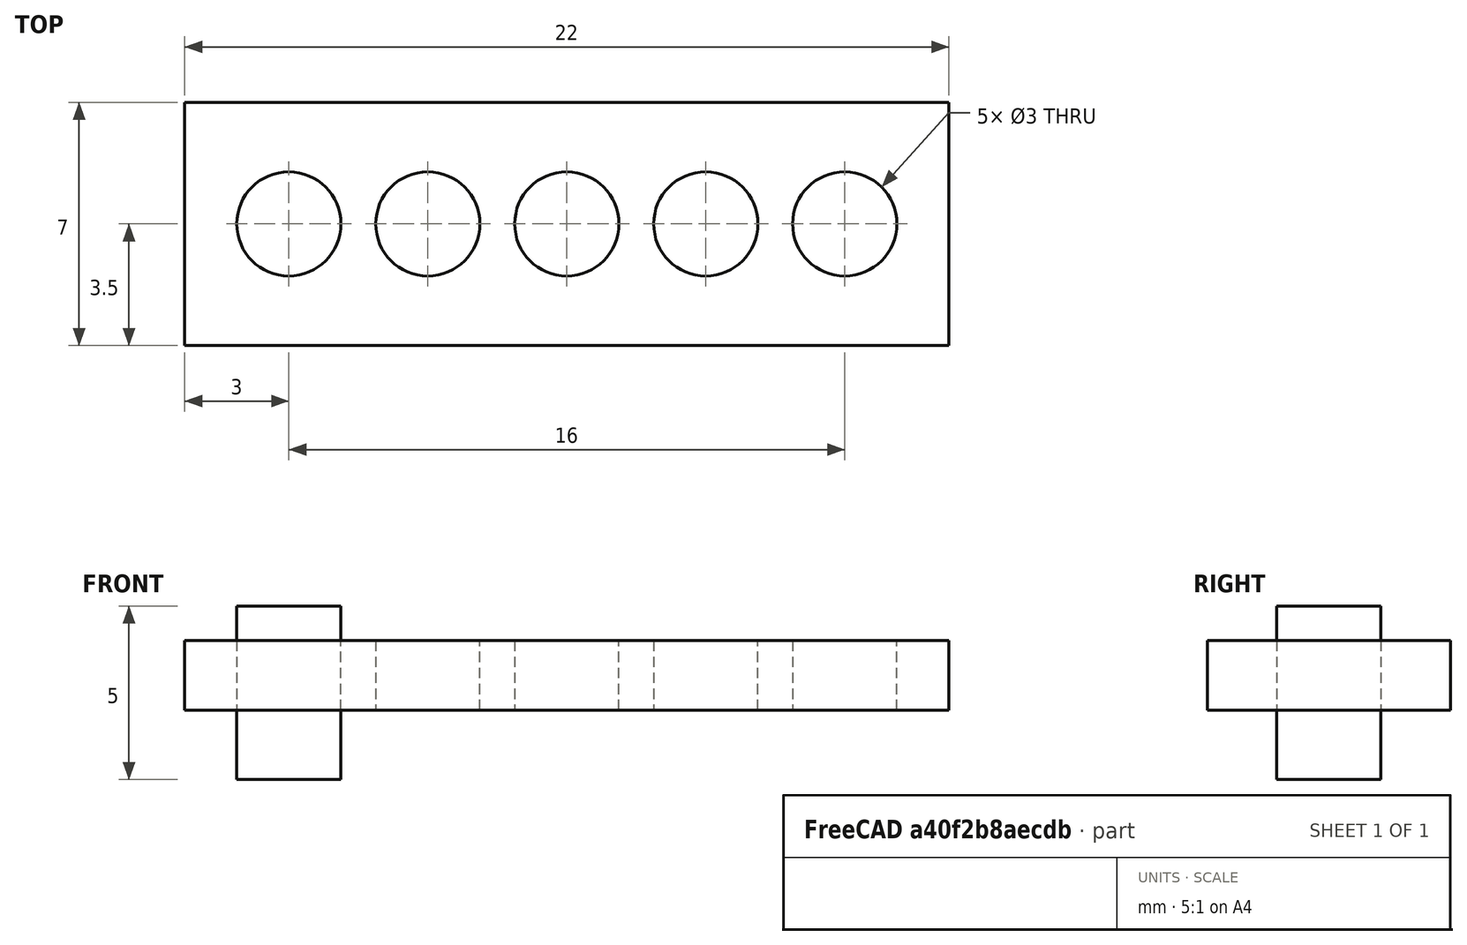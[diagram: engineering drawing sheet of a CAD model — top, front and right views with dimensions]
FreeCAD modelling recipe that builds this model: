
FCSTD DOCUMENT  (FreeCAD 0.21R33694 (Git))
Label: OJT1_T010R09_6cercles_forats
License: All rights reserved
LicenseURL: http://en.wikipedia.org/wiki/All_rights_reserved
objects: Part::Cylinder×1, Part::FeaturePython×1, Part::Box×1, Part::Cut×1
note: 3 computed .brp shape members not serialized (recipe doc carries the construction recipe); baked Part::Feature solids carry a one-line shape summary decoded from their .brp

FEATURE [Part::Cylinder] Cylinder
  Angle = 360
  AttacherType = Attacher::AttachEngine3D
  FirstAngle = 0
  Height = 5
  Radius = 1.5
  SecondAngle = 0
FEATURE [Part::FeaturePython] Array  # Draft array (typed FeaturePython)
  AlwaysSyncPlacement = false
  Angle = 360
  ArrayType = 0
  Axis = (0,0,1)
  Base = -> Cylinder
  Center = (0,0,0)
  Count = 5
  ExpandArray = false
  Fuse = false
  IntervalAxis = (0,0,0)
  IntervalX = (4,0,0)
  IntervalY = (0,100,0)
  IntervalZ = (0,0,100)
  NumberCircles = 3
  NumberPolar = 5
  NumberX = 5
  NumberY = 1
  NumberZ = 1
  PlacementList = 5 placements: arithmetic series from (0,0,0) step (4,0,0) to (16,0,0)
  RadialDistance = 50
  ScaleList = (5) [(1,1,1),(1,1,1),(1,1,1),(1,1,1),(1,1,1)]
  Symmetry = 1
  TangentialDistance = 25
FEATURE [Part::Box] Box  label="Cube"
  AttacherType = Attacher::AttachEngine3D
  Height = 2
  Length = 22
  Placement = pos=(-3,-3.5,2) rot=(0,0,1;0rad)
  Width = 7
FEATURE [Part::Cut] Cut
  Base = -> Box
  Refine = true
  Tool = -> Array
